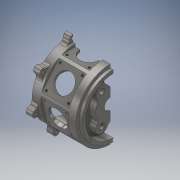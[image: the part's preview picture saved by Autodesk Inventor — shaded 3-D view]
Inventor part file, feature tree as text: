
AUTODESK INVENTOR PART (.ipt)
format: ipt  version: 2018 (Build 220112000, 112)  size: 584,192 bytes
history: native  units: mm
features: sketch x10, extrude x10, hole x4, pattern_circular x2, direct_edit x1, chamfer x1, other x1, revolve x1, projected_geometry x1
ambient origin geometry x8: Origin, YZ Plane, XZ Plane, XY Plane, X Axis, Y Axis, Z Axis, Center Point
bodies: Solid1 (feature_tree)
feature tree (31):
  sketch  "Sketch1"  dims[d0=100.0mm d1=90.0mm]
  extrude  "Extrusion1"  Depth=90.0mm
  extrude  "Extrusion2"  Depth=67.0mm TaperAngle=0.0deg
  extrude  "Extrusion3"  Depth=4.07mm
  extrude  "Extrusion4"  Depth=13.0mm TaperAngle=0.0deg
  extrude  "Extrusion5"  Depth=18.0mm
  direct_edit  "Direct Edit1"
  extrude  "Extrusion6"  Depth=12.0mm
  extrude  "Extrusion7"  Depth=30.0mm TaperAngle=360.0deg
  chamfer  "Chamfer1"  Distance=9.0mm
  extrude  "Extrusion8"  Depth=5.0mm
  sketch  "Sketch8"  dims[d28=8.0mm d29=30.0mm d31=360.0deg]
  extrude  "Extrusion9"  Depth=10.0mm TaperAngle=0.0deg
  hole  "Hole1"  [1 undecoded]
  extrude  "Extrusion10"  Depth=5.0mm TaperAngle=0.0deg
  hole  "Hole2"  [1 undecoded]
  hole  "Hole3"  [1 undecoded]
  other  "Work Axis1"
  pattern_circular  "Circular Pattern1"  [2 undecoded]
  hole  "Hole4"  [1 undecoded]
  pattern_circular  "Circular Pattern2"  [2 undecoded]
  sketch  "Sketch2"  dims[d2=80.0mm d3=67.0mm d4=0.0mm]
  sketch  "Sketch4"  dims[d5=4.07mm d6=0.0mm d7=85.0mm]
  sketch  "Sketch5"  dims[d8=50.0mm d9=0.0mm d10=13.0mm d11=0.0mm]
  sketch  "Sketch6"  dims[d12=43.0mm d22=21.5mm d25=18.0mm]
  sketch  "Sketch7"  dims[d26=25.0mm d27=12.0mm]
  sketch  "Sketch9"  dims[d33=21.5mm]
  sketch  "Sketch10"  dims[d34=21.5mm d35=9.0mm d36=0.0mm]
  sketch  "Sketch11"  dims[d37=-15.707963mm d38=35.0mm d39=10.0mm d40=0.0mm d41=17.35mm d42=17.0mm d43=0.0mm d44=2.0mm d45=2.0mm d46=45.0deg d47=40.0mm d48=10.43mm d49=46.0mm d50=39.19mm d51=0.0mm d53=39.19mm d54=0.0mm d55=27.0mm d57=19.595mm d58=32.0mm d59=32.0mm d60=3.242mm d61=8.0mm d62=3.023mm d63=2.0mm d64=14.3117mm d65=11.8mm d66=20.594885mm d67=20.0mm d69=13.0mm d70=9.0mm d71=0.0mm d72=10.0mm d73=10.0mm d74=4.134mm d75=10.0mm d76=3.023mm d77=2.0mm d78=14.3117mm d79=14.2mm d80=20.594885mm d81=46.0mm d82=3.242mm d83=8.0mm d84=3.023mm d85=2.0mm d86=14.3117mm d87=10.8mm d88=20.594885mm d89=70.0mm d90=360.0deg d92=85.0mm d93=3.242mm d94=8.0mm d95=3.023mm d96=2.0mm d97=14.3117mm d98=13.3mm d99=20.594885mm d100=70.0mm d101=360.0deg d103=55.0mm d104=5.0mm]
  revolve  "Rotate1"  [1 undecoded]
  projected_geometry  "Project Cut Edges1"
note: 9 required parameter values undecoded (feature->parameter linkage not recoverable at this tier; creation-order binding heuristic only, values carry confidence <= 0.55)